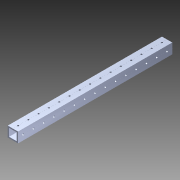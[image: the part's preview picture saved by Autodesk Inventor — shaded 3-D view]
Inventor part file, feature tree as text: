
AUTODESK INVENTOR PART (.ipt)
format: ipt  version: 2014 (Build 180170000, 170)  size: 1,183,232 bytes
history: native  units: in
note: dims shown in document units (in); Inventor stores cm internally (conversion verified against a paired STEP export)
features: pattern_circular x1, other x1, plane x1, extrude x1, imported_body x1, sketch x1
ambient origin geometry x8: Origin, YZ Plane, XZ Plane, XY Plane, X Axis, Y Axis, Z Axis, Center Point
bodies: Body1 (feature_tree)
feature tree (6):
  pattern_circular  "CirPattern2"
  other  "217-3426-STEP1"
  plane  "Work Plane1"
  extrude  "Extrusion1"  Depth=3937.0079in TaperAngle=0.0deg
  imported_body  "Base1"
  sketch  "Sketch1"  dims[d0=-15.0in d1=3937.0079in d2=0.0in]
